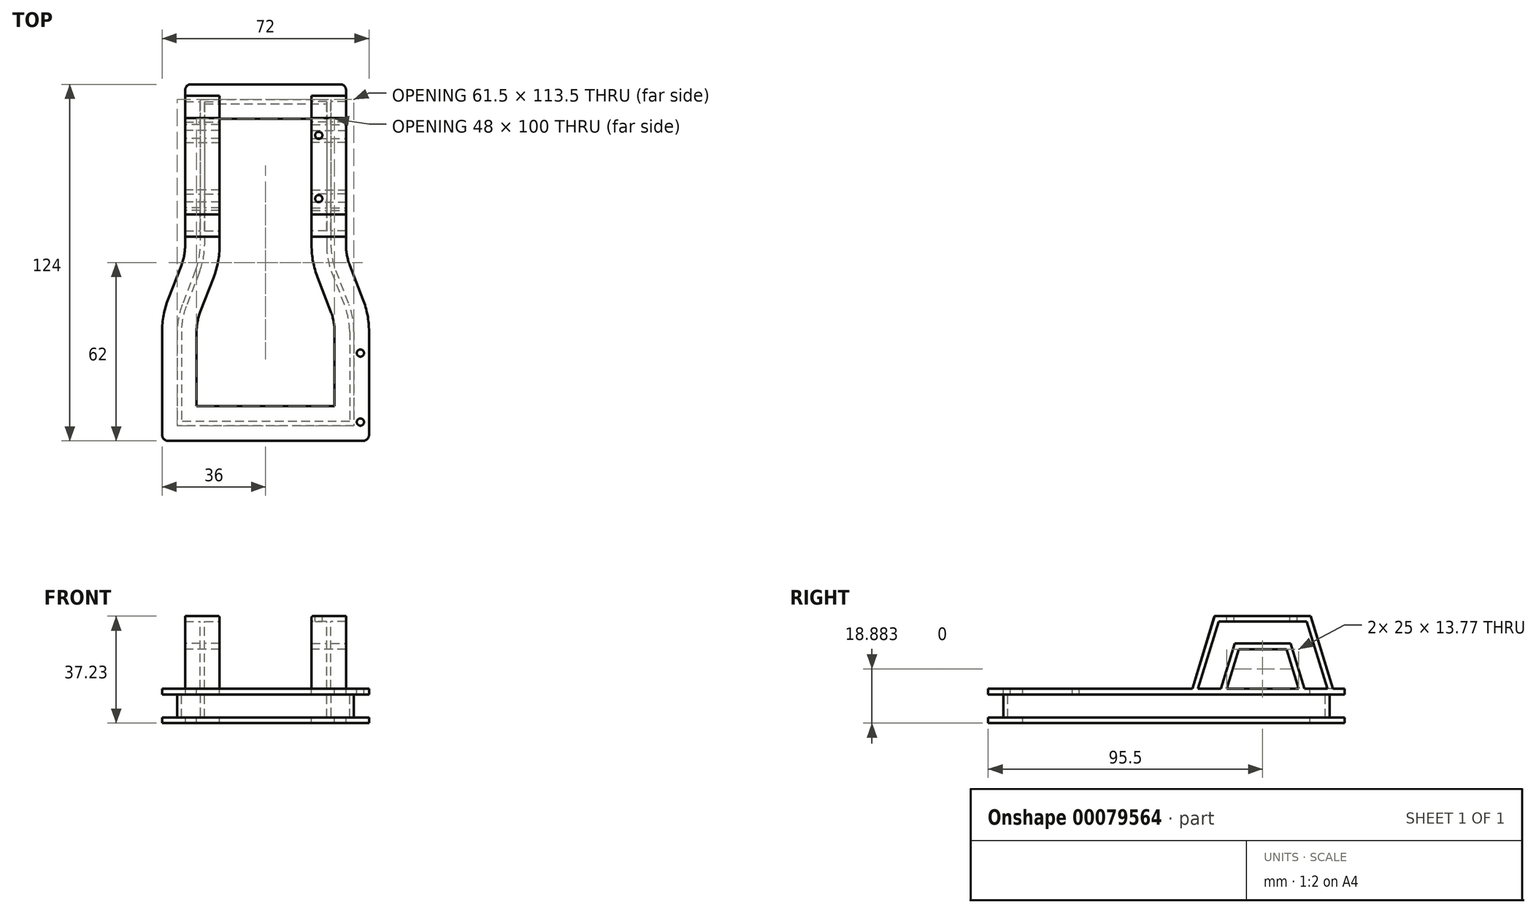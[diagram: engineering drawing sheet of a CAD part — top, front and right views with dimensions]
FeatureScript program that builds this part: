
annotation { "Feature Type Name" : "Feature", "Feature Type Description" : "" }
export const myFeature = defineFeature(function(context is Context, id is Id, definition is map)
    precondition{}
    {
        {
            var Q0;
            Q0=qCreatedBy(makeId("Top.planeOp"),FACE);
            var sketch = newSketch(context, id + "F0", { "sketchPlane" : qUnion([Q0])});
            skLineSegment(sketch, "E0", {"start": v(0, 0) * mm, "end": v(22, 0) * mm});
            skLineSegment(sketch, "E1", {"start": v(22, 0) * mm, "end": v(22, -50) * mm});
            skLineSegment(sketch, "E2", {"start": v(30, -80) * mm, "end": v(30, -112) * mm});
            skLineSegment(sketch, "E3", {"start": v(30, -112) * mm, "end": v(0, -112) * mm});
            skLineSegment(sketch, "E4", {"start": v(23.69, -59.03) * mm, "end": v(28.31, -70.97) * mm});
            skPoint(sketch, "E5.visualSharp", {"position": v(22, -54.67) * mm});
            skArc(sketch, "E5.filletArc", {"start": v(22, -50) * mm, "mid": v(22.43, -54.6) * mm, "end": v(23.69, -59.03) * mm});
            skPoint(sketch, "E6.visualSharp", {"position": v(30, -75.33) * mm});
            skArc(sketch, "E6.filletArc", {"start": v(30, -80) * mm, "mid": v(29.57, -75.4) * mm, "end": v(28.31, -70.97) * mm});
            skSolve(sketch);
        }
        {
            var Q0;
            Q0=qCreatedBy(makeId("Right.planeOp"),FACE);
            var sketch = newSketch(context, id + "F1", { "sketchPlane" : qUnion([Q0])});
            skLineSegment(sketch, "E7.bottom", {"start": v(6, 0) * mm, "end": v(-6, 0) * mm});
            skLineSegment(sketch, "E7.top", {"start": v(6, 2) * mm, "end": v(0.75, 2) * mm});
            skLineSegment(sketch, "E7.left", {"start": v(6, 0) * mm, "end": v(6, 2) * mm});
            skLineSegment(sketch, "E7.right", {"start": v(-6, 0) * mm, "end": v(-6, 2) * mm});
            skLineSegment(sketch, "E8.left", {"start": v(0.75, 2) * mm, "end": v(0.75, 10) * mm});
            skLineSegment(sketch, "E8.right", {"start": v(-0.75, 2) * mm, "end": v(-0.75, 10) * mm});
            skLineSegment(sketch, "E9.bottom", {"start": v(-6, 10) * mm, "end": v(-0.75, 10) * mm});
            skLineSegment(sketch, "E9.top", {"start": v(-6, 12) * mm, "end": v(6, 12) * mm});
            skLineSegment(sketch, "E9.left", {"start": v(-6, 10) * mm, "end": v(-6, 12) * mm});
            skLineSegment(sketch, "E9.right", {"start": v(6, 10) * mm, "end": v(6, 12) * mm});
            skLineSegment(sketch, "E10.trimOffspring", {"start": v(0.75, 10) * mm, "end": v(6, 10) * mm});
            skLineSegment(sketch, "E11.trimOffspring", {"start": v(-0.75, 2) * mm, "end": v(-6, 2) * mm});
            skSolve(sketch);
        }
        {
            var Q0;
            Q0=makeQuery(id+"F1.imprint","IMPRINT",FACE,{"disambiguationData":[TD([[makeQuery(id+"F1.imprint","IMPRINT",EDGE,{"derivedFrom":sQuery(id+"F1.wireOp",EDGE,"E7.bottom")}),-1.0]])]});
            var Q1;
            Q1=sQuery(id+"F0.wireOp",EDGE,"E1");
            var Q2;
            Q2=sQuery(id+"F0.wireOp",EDGE,"E0");
            var Q3;
            Q3=sQuery(id+"F0.wireOp",EDGE,"E5.filletArc");
            var Q4;
            Q4=sQuery(id+"F0.wireOp",EDGE,"E4");
            var Q5;
            Q5=sQuery(id+"F0.wireOp",EDGE,"E6.filletArc");
            var Q6;
            Q6=sQuery(id+"F0.wireOp",EDGE,"E2");
            var Q7;
            Q7=sQuery(id+"F0.wireOp",EDGE,"E3");
            sweep(context, id + "F2", {"profiles" : qUnion([Q0]), "path" : qUnion([Q1, Q2, Q3, Q4, Q5, Q6, Q7])});
        }
        {
            var Q0;
            Q0=qCreatedBy(makeId("Right.planeOp"),FACE);
            cPlane(context, id + "F3", {"entities" : qUnion([Q0]), "cplaneType" : CPlaneType.OFFSET, "offset" : 22 * mm, "width" : 150 * mm, "height" : 150 * mm});
        }
        {
            var Q0;
            Q0=qCreatedBy(id+"F3.planeOp",FACE);
            var sketch = newSketch(context, id + "F4", { "sketchPlane" : qUnion([Q0])});
            skLineSegment(sketch, "E12.0", {"start": v(-6, 12) * mm, "end": v(-50, 12) * mm, "construction": true});
            skLineSegment(sketch, "E13.0", {"start": v(6, 12) * mm, "end": v(-6, 12) * mm, "construction": true});
            skLineSegment(sketch, "E14.0", {"start": v(-50, 12) * mm, "end": v(-61.2, 12) * mm, "construction": true});
            skLineSegment(sketch, "E15", {"start": v(-4, 12) * mm, "end": v(-10, 31.5) * mm});
            skLineSegment(sketch, "E16", {"start": v(-35, 31.5) * mm, "end": v(-41, 12) * mm});
            skLineSegment(sketch, "E17", {"start": v(-10, 31.5) * mm, "end": v(-16.25, 31.5) * mm});
            skLineSegment(sketch, "E18", {"start": v(-16.25, 31.5) * mm, "end": v(-22.5, 31.5) * mm});
            skLineSegment(sketch, "E19", {"start": v(-22.5, 31.5) * mm, "end": v(-28.75, 31.5) * mm});
            skLineSegment(sketch, "E20", {"start": v(-28.75, 31.5) * mm, "end": v(-35, 31.5) * mm});
            skSolve(sketch);
        }
        {
            var Q0;
            Q0=makeQuery(id+"F2.opSweep","SWEPT_FACE",FACE,{"disambiguationData":[OSD([sQuery(id+"F0.wireOp",EDGE,"E0"),sQuery(id+"F1.wireOp",EDGE,"E9.top")])]});
            var sketch = newSketch(context, id + "F5", { "sketchPlane" : qUnion([Q0])});
            skLineSegment(sketch, "E21.bottom", {"start": v(28, 2) * mm, "end": v(16, 2) * mm});
            skLineSegment(sketch, "E21.top", {"start": v(28, 0) * mm, "end": v(22.75, 0) * mm});
            skLineSegment(sketch, "E21.left", {"start": v(28, 2) * mm, "end": v(28, 0) * mm});
            skLineSegment(sketch, "E21.right", {"start": v(16, 2) * mm, "end": v(16, 0) * mm});
            skLineSegment(sketch, "E22.bottom", {"start": v(16, -8) * mm, "end": v(21.25, -8) * mm});
            skLineSegment(sketch, "E22.top", {"start": v(16, -10) * mm, "end": v(28, -10) * mm});
            skLineSegment(sketch, "E22.left", {"start": v(16, -8) * mm, "end": v(16, -10) * mm});
            skLineSegment(sketch, "E22.right", {"start": v(28, -8) * mm, "end": v(28, -10) * mm});
            skLineSegment(sketch, "E23.left", {"start": v(22.75, -8) * mm, "end": v(22.75, 0) * mm});
            skLineSegment(sketch, "E23.right", {"start": v(21.25, -8) * mm, "end": v(21.25, 0) * mm});
            skLineSegment(sketch, "E24.trimOffspring", {"start": v(22.75, -8) * mm, "end": v(28, -8) * mm});
            skLineSegment(sketch, "E25.trimOffspring", {"start": v(21.25, 0) * mm, "end": v(16, 0) * mm});
            skLineSegment(sketch, "E26", {"start": v(35.77, -22.5) * mm, "end": v(9.16, -22.5) * mm, "construction": true});
            skLineSegment(sketch, "E27", {"start": v(22, -4) * mm, "end": v(22, -22.5) * mm, "construction": true});
            skPoint(sketch, "E27.startSnap0", {"position": v(21.25, -4) * mm});
            skPoint(sketch, "E28.0", {"position": v(22, -41) * mm});
            skLineSegment(sketch, "E29", {"start": v(22, -22.5) * mm, "end": v(22, -41) * mm, "construction": true});
            skLineSegment(sketch, "E30.MirrorCS", {"start": v(21.25, -45) * mm, "end": v(16, -45) * mm});
            skLineSegment(sketch, "E31.MirrorCS", {"start": v(16, -47) * mm, "end": v(16, -45) * mm});
            skLineSegment(sketch, "E32.MirrorCS", {"start": v(28, -47) * mm, "end": v(16, -47) * mm});
            skLineSegment(sketch, "E33.MirrorCS", {"start": v(28, -47) * mm, "end": v(28, -45) * mm});
            skLineSegment(sketch, "E34.MirrorCS", {"start": v(28, -45) * mm, "end": v(22.75, -45) * mm});
            skLineSegment(sketch, "E35.MirrorCS", {"start": v(22.75, -37) * mm, "end": v(28, -37) * mm});
            skLineSegment(sketch, "E36.MirrorCS", {"start": v(22.75, -37) * mm, "end": v(22.75, -45) * mm});
            skLineSegment(sketch, "E37.MirrorCS", {"start": v(21.25, -37) * mm, "end": v(21.25, -45) * mm});
            skLineSegment(sketch, "E38.MirrorCS", {"start": v(16, -37) * mm, "end": v(21.25, -37) * mm});
            skLineSegment(sketch, "E39.MirrorCS", {"start": v(16, -37) * mm, "end": v(16, -35) * mm});
            skLineSegment(sketch, "E40.MirrorCS", {"start": v(16, -35) * mm, "end": v(28, -35) * mm});
            skLineSegment(sketch, "E41.MirrorCS", {"start": v(28, -37) * mm, "end": v(28, -35) * mm});
            skSolve(sketch);
        }
        {
            var Q0;
            Q0=makeQuery(id+"F5.imprint","IMPRINT",FACE,{"disambiguationData":[TD([[makeQuery(id+"F5.imprint","IMPRINT",EDGE,{"derivedFrom":sQuery(id+"F5.wireOp",EDGE,"E21.bottom")}),1.0]])]});
            var Q1;
            Q1=sQuery(id+"F4.wireOp",EDGE,"E15");
            var Q2;
            Q2=sQuery(id+"F4.wireOp",EDGE,"E17");
            var Q3;
            Q3=sQuery(id+"F4.wireOp",EDGE,"E18");
            var Q4;
            Q4=sQuery(id+"F4.wireOp",EDGE,"E19");
            sweep(context, id + "F6", {"operationType" : NewBodyOperationType.ADD, "profiles" : qUnion([Q0]), "path" : qUnion([Q1, Q2, Q3, Q4])});
        }
        {
            var Q0;
            Q0=makeQuery(id+"F5.imprint","IMPRINT",FACE,{"disambiguationData":[TD([[makeQuery(id+"F5.imprint","IMPRINT",EDGE,{"derivedFrom":sQuery(id+"F5.wireOp",EDGE,"E30.MirrorCS")}),1.0]])]});
            var Q1;
            Q1=sQuery(id+"F4.wireOp",EDGE,"E16");
            var Q2;
            Q2=sQuery(id+"F4.wireOp",EDGE,"E20");
            var Q3;
            Q3=sQuery(id+"F4.wireOp",EDGE,"E19");
            var Q4;
            Q4=sQuery(id+"F4.wireOp",EDGE,"E18");
            sweep(context, id + "F7", {"operationType" : NewBodyOperationType.ADD, "profiles" : qUnion([Q0]), "path" : qUnion([Q1, Q2, Q3, Q4])});
        }
        {
            var Q0;
            Q0=makeQuery(id+"F2.opSweep","SWEPT_BODY",BODY,{"disambiguationData":[OSD([sQuery(id+"F0.wireOp",EDGE,"E0"),sQuery(id+"F1.wireOp",EDGE,"E7.bottom"),sQuery(id+"F1.wireOp",EDGE,"E7.top"),sQuery(id+"F1.wireOp",EDGE,"E7.left"),sQuery(id+"F1.wireOp",EDGE,"E7.right"),sQuery(id+"F1.wireOp",EDGE,"E8.left"),sQuery(id+"F1.wireOp",EDGE,"E8.right"),sQuery(id+"F1.wireOp",EDGE,"E9.bottom"),sQuery(id+"F1.wireOp",EDGE,"E9.top"),sQuery(id+"F1.wireOp",EDGE,"E9.left"),sQuery(id+"F1.wireOp",EDGE,"E9.right"),sQuery(id+"F1.wireOp",EDGE,"E10.trimOffspring"),sQuery(id+"F1.wireOp",EDGE,"E11.trimOffspring")])]});
            var Q1;
            Q1=qCreatedBy(makeId("Right.planeOp"),FACE);
            mirror(context, id + "F8", {"operationType" : NewBodyOperationType.ADD, "entities" : qUnion([Q0]), "mirrorPlane" : qUnion([Q1])});
        }
        {
            var Q0;
            Q0=makeQuery(id+"F7.boolean.opBoolean","MERGE",FACE,{"derivedFrom":[makeQuery(id+"F6.opSweep","SWEPT_FACE",FACE,{"disambiguationData":[OSD([sQuery(id+"F4.wireOp",EDGE,"E19"),sQuery(id+"F5.wireOp",EDGE,"E21.bottom")])]}),makeQuery(id+"F7.opSweep","SWEPT_FACE",FACE,{"disambiguationData":[OSD([sQuery(id+"F4.wireOp",EDGE,"E18"),sQuery(id+"F5.wireOp",EDGE,"E32.MirrorCS")])]})]});
            var sketch = newSketch(context, id + "F9", { "sketchPlane" : qUnion([Q0])});
            skPoint(sketch, "E42", {"position": v(18.5, -11.76) * mm});
            skPoint(sketch, "E43", {"position": v(18.5, -33.76) * mm});
            skSolve(sketch);
        }
        {
            var Q0;
            Q0=sQuery(id+"F9.wireOp",VERTEX,"E42");
            var Q1;
            Q1=sQuery(id+"F9.wireOp",VERTEX,"E43");
            var Q2;
            Q2=makeQuery(id+"F2.opSweep","SWEPT_BODY",BODY,{"disambiguationData":[OSD([sQuery(id+"F0.wireOp",EDGE,"E0"),sQuery(id+"F1.wireOp",EDGE,"E7.bottom"),sQuery(id+"F1.wireOp",EDGE,"E7.top"),sQuery(id+"F1.wireOp",EDGE,"E7.left"),sQuery(id+"F1.wireOp",EDGE,"E7.right"),sQuery(id+"F1.wireOp",EDGE,"E8.left"),sQuery(id+"F1.wireOp",EDGE,"E8.right"),sQuery(id+"F1.wireOp",EDGE,"E9.bottom"),sQuery(id+"F1.wireOp",EDGE,"E9.top"),sQuery(id+"F1.wireOp",EDGE,"E9.left"),sQuery(id+"F1.wireOp",EDGE,"E9.right"),sQuery(id+"F1.wireOp",EDGE,"E10.trimOffspring"),sQuery(id+"F1.wireOp",EDGE,"E11.trimOffspring")])]});
            hole(context, id + "F10", {"style" : HoleStyle.SIMPLE, "endStyle" : HoleEndStyle.BLIND, "holeDiameter" : 2.5 * mm, "holeDepth" : 3 * mm, "locations" : qUnion([Q0, Q1]), "scope" : qUnion([Q2])});
        }
        {
            var Q0;
            {var subQ7=sQuery(id+"F1.wireOp",EDGE,"E9.left");var subQ13=sQuery(id+"F0.wireOp",EDGE,"E2");var subQ15=sQuery(id+"F1.wireOp",EDGE,"E9.top");var subQ22=makeQuery(id+"F2.opSweep","SWEPT_FACE",FACE,{"disambiguationData":[OSD([subQ13,subQ7])]});var subQ27=makeQuery(id+"F7.boolean.opBoolean","SPLIT",FACE,{"disambiguationData":[TD([subQ22])],"derivedFrom":makeQuery(id+"F6.boolean.opBoolean","SPLIT",FACE,{"disambiguationData":[TD([subQ22])],"derivedFrom":makeQuery(id+"F2.opSweep","SWEPT_FACE",FACE,{"disambiguationData":[OSD([sQuery(id+"F0.wireOp",EDGE,"E0"),subQ15])]})})});Q0=makeQuery(id+"F8.boolean.opBoolean","MERGE",FACE,{"derivedFrom":[subQ27,makeQuery(id+"F8.opPattern","COPY",FACE,{"derivedFrom":subQ27,"instanceName":"1"})]});}
            var sketch = newSketch(context, id + "F11", { "sketchPlane" : qUnion([Q0])});
            skPoint(sketch, "E44", {"position": v(33, -111.5) * mm});
            skPoint(sketch, "E45", {"position": v(33, -87.5) * mm});
            skSolve(sketch);
        }
        {
            var Q0;
            Q0=sQuery(id+"F11.wireOp",VERTEX,"E45");
            var Q1;
            Q1=sQuery(id+"F11.wireOp",VERTEX,"E44");
            var Q2;
            Q2=makeQuery(id+"F2.opSweep","SWEPT_BODY",BODY,{"disambiguationData":[OSD([sQuery(id+"F0.wireOp",EDGE,"E0"),sQuery(id+"F1.wireOp",EDGE,"E7.bottom"),sQuery(id+"F1.wireOp",EDGE,"E7.top"),sQuery(id+"F1.wireOp",EDGE,"E7.left"),sQuery(id+"F1.wireOp",EDGE,"E7.right"),sQuery(id+"F1.wireOp",EDGE,"E8.left"),sQuery(id+"F1.wireOp",EDGE,"E8.right"),sQuery(id+"F1.wireOp",EDGE,"E9.bottom"),sQuery(id+"F1.wireOp",EDGE,"E9.top"),sQuery(id+"F1.wireOp",EDGE,"E9.left"),sQuery(id+"F1.wireOp",EDGE,"E9.right"),sQuery(id+"F1.wireOp",EDGE,"E10.trimOffspring"),sQuery(id+"F1.wireOp",EDGE,"E11.trimOffspring")])]});
            hole(context, id + "F12", {"style" : HoleStyle.SIMPLE, "endStyle" : HoleEndStyle.BLIND, "holeDiameter" : 2.5 * mm, "holeDepth" : 3 * mm, "locations" : qUnion([Q0, Q1]), "scope" : qUnion([Q2])});
        }
        {
            var Q0;
            Q0=makeQuery(id+"F2.opSweep","MID_CAP_EDGE",EDGE,{"disambiguationData":[OSD([sQuery(id+"F0.wireOp",VERTEX,"E3.start"),sQuery(id+"F1.wireOp",EDGE,"E9.right")])],"capPos":6.0});
            var Q1;
            Q1=makeQuery(id+"F2.opSweep","MID_CAP_EDGE",EDGE,{"disambiguationData":[OSD([sQuery(id+"F0.wireOp",VERTEX,"E3.start"),sQuery(id+"F1.wireOp",EDGE,"E7.left")])],"capPos":6.0});
            var Q2;
            Q2=makeQuery(id+"F2.opSweep","MID_CAP_EDGE",EDGE,{"disambiguationData":[OSD([sQuery(id+"F0.wireOp",VERTEX,"E0.end"),sQuery(id+"F1.wireOp",EDGE,"E7.left")])],"capPos":1.0});
            var Q3;
            Q3=makeQuery(id+"F2.opSweep","MID_CAP_EDGE",EDGE,{"disambiguationData":[OSD([sQuery(id+"F0.wireOp",VERTEX,"E0.end"),sQuery(id+"F1.wireOp",EDGE,"E9.right")])],"capPos":1.0});
            fillet(context, id + "F13", {"entities" : qUnion([Q0, Q1, Q2, Q3]), "radius" : 2 * mm, "tangentPropagation" : true, "allowEdgeOverflow" : false});
        }
        {
            var Q0;
            Q0=makeQuery(id+"F7.boolean.opBoolean","MERGE",EDGE,{"derivedFrom":[makeQuery(id+"F6.opSweep","SWEPT_EDGE",EDGE,{"disambiguationData":[OSD([sQuery(id+"F4.wireOp",EDGE,"E17"),sQuery(id+"F5.wireOp",EDGE,"E21.bottom"),sQuery(id+"F5.wireOp",EDGE,"E21.right")])]}),makeQuery(id+"F7.opSweep","SWEPT_EDGE",EDGE,{"disambiguationData":[OSD([sQuery(id+"F0.wireOp",EDGE,"E1"),sQuery(id+"F1.wireOp",EDGE,"E9.top"),sQuery(id+"F1.wireOp",EDGE,"E9.left"),sQuery(id+"F4.wireOp",EDGE,"E20"),sQuery(id+"F5.wireOp",EDGE,"E31.MirrorCS"),sQuery(id+"F5.wireOp",EDGE,"E32.MirrorCS")])]})]});
            fillet(context, id + "F14", {"entities" : qUnion([Q0]), "radius" : 0.5 * mm, "tangentPropagation" : true, "allowEdgeOverflow" : false});
        }
        {
            var Q0;
            Q0=makeQuery(id+"F8.opPattern","COPY",EDGE,{"derivedFrom":makeQuery(id+"F2.opSweep","MID_CAP_EDGE",EDGE,{"disambiguationData":[OSD([sQuery(id+"F0.wireOp",VERTEX,"E3.start"),sQuery(id+"F1.wireOp",EDGE,"E9.right")])],"capPos":6.0}),"instanceName":"1"});
            var Q1;
            Q1=makeQuery(id+"F8.opPattern","COPY",EDGE,{"derivedFrom":makeQuery(id+"F2.opSweep","MID_CAP_EDGE",EDGE,{"disambiguationData":[OSD([sQuery(id+"F0.wireOp",VERTEX,"E3.start"),sQuery(id+"F1.wireOp",EDGE,"E7.left")])],"capPos":6.0}),"instanceName":"1"});
            var Q2;
            Q2=makeQuery(id+"F8.opPattern","COPY",EDGE,{"derivedFrom":makeQuery(id+"F2.opSweep","MID_CAP_EDGE",EDGE,{"disambiguationData":[OSD([sQuery(id+"F0.wireOp",VERTEX,"E0.end"),sQuery(id+"F1.wireOp",EDGE,"E9.right")])],"capPos":1.0}),"instanceName":"1"});
            var Q3;
            Q3=makeQuery(id+"F8.opPattern","COPY",EDGE,{"derivedFrom":makeQuery(id+"F2.opSweep","MID_CAP_EDGE",EDGE,{"disambiguationData":[OSD([sQuery(id+"F0.wireOp",VERTEX,"E0.end"),sQuery(id+"F1.wireOp",EDGE,"E7.left")])],"capPos":1.0}),"instanceName":"1"});
            fillet(context, id + "F15", {"entities" : qUnion([Q0, Q1, Q2, Q3]), "radius" : 2 * mm, "tangentPropagation" : true, "allowEdgeOverflow" : false});
        }
        {
            var Q0;
            Q0=makeQuery(id+"F8.opPattern","COPY",EDGE,{"derivedFrom":makeQuery(id+"F7.boolean.opBoolean","MERGE",EDGE,{"derivedFrom":[makeQuery(id+"F6.opSweep","SWEPT_EDGE",EDGE,{"disambiguationData":[OSD([sQuery(id+"F4.wireOp",EDGE,"E17"),sQuery(id+"F5.wireOp",EDGE,"E21.bottom"),sQuery(id+"F5.wireOp",EDGE,"E21.right")])]}),makeQuery(id+"F7.opSweep","SWEPT_EDGE",EDGE,{"disambiguationData":[OSD([sQuery(id+"F0.wireOp",EDGE,"E1"),sQuery(id+"F1.wireOp",EDGE,"E9.top"),sQuery(id+"F1.wireOp",EDGE,"E9.left"),sQuery(id+"F4.wireOp",EDGE,"E20"),sQuery(id+"F5.wireOp",EDGE,"E31.MirrorCS"),sQuery(id+"F5.wireOp",EDGE,"E32.MirrorCS")])]})]}),"instanceName":"1"});
            fillet(context, id + "F16", {"entities" : qUnion([Q0]), "radius" : .5 * mm, "tangentPropagation" : true, "allowEdgeOverflow" : false});
        }
    });
